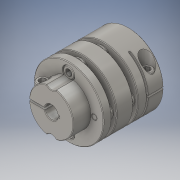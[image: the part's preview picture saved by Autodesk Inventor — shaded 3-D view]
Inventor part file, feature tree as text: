
AUTODESK INVENTOR PART (.ipt)
format: ipt  version: 2016 (Build 200138000, 138)  size: 1,616,896 bytes
history: native  units: in
note: dims shown in document units (in); Inventor stores cm internally (conversion verified against a paired STEP export)
features: other x7, chamfer x5, pattern_circular x1
ambient origin geometry x8: Origin, YZ Plane, XZ Plane, XY Plane, X Axis, Y Axis, Z Axis, Center Point
bodies: Solid1 (feature_tree), Solid2 (feature_tree), Solid3 (feature_tree), Solid4 (feature_tree), Solid5 (feature_tree), Solid6 (feature_tree), Solid7 (feature_tree), Solid8 (feature_tree), Solid9 (feature_tree), Solid10 (feature_tree), Solid11 (feature_tree), Solid12 (feature_tree), Solid13 (feature_tree)
feature tree (13):
  chamfer  "Chamfer3"  [1 undecoded]
  pattern_circular  "CirPattern2"
  chamfer  "Chamfer10"  [1 undecoded]
  chamfer  "Chamfer11"  [1 undecoded]
  other  "Boss-Extrude4"
  chamfer  "Chamfer5"  [1 undecoded]
  other  "CirPattern3[1]"
  other  "CirPattern3[2]"
  other  "CirPattern3[3]"
  other  "CirPattern3[5]"
  chamfer  "Chamfer7"  [1 undecoded]
  other  "LPattern2"
  other  "Cut-Extrude32"
note: 5 required parameter values undecoded (feature->parameter linkage not recoverable at this tier; creation-order binding heuristic only, values carry confidence <= 0.55)
